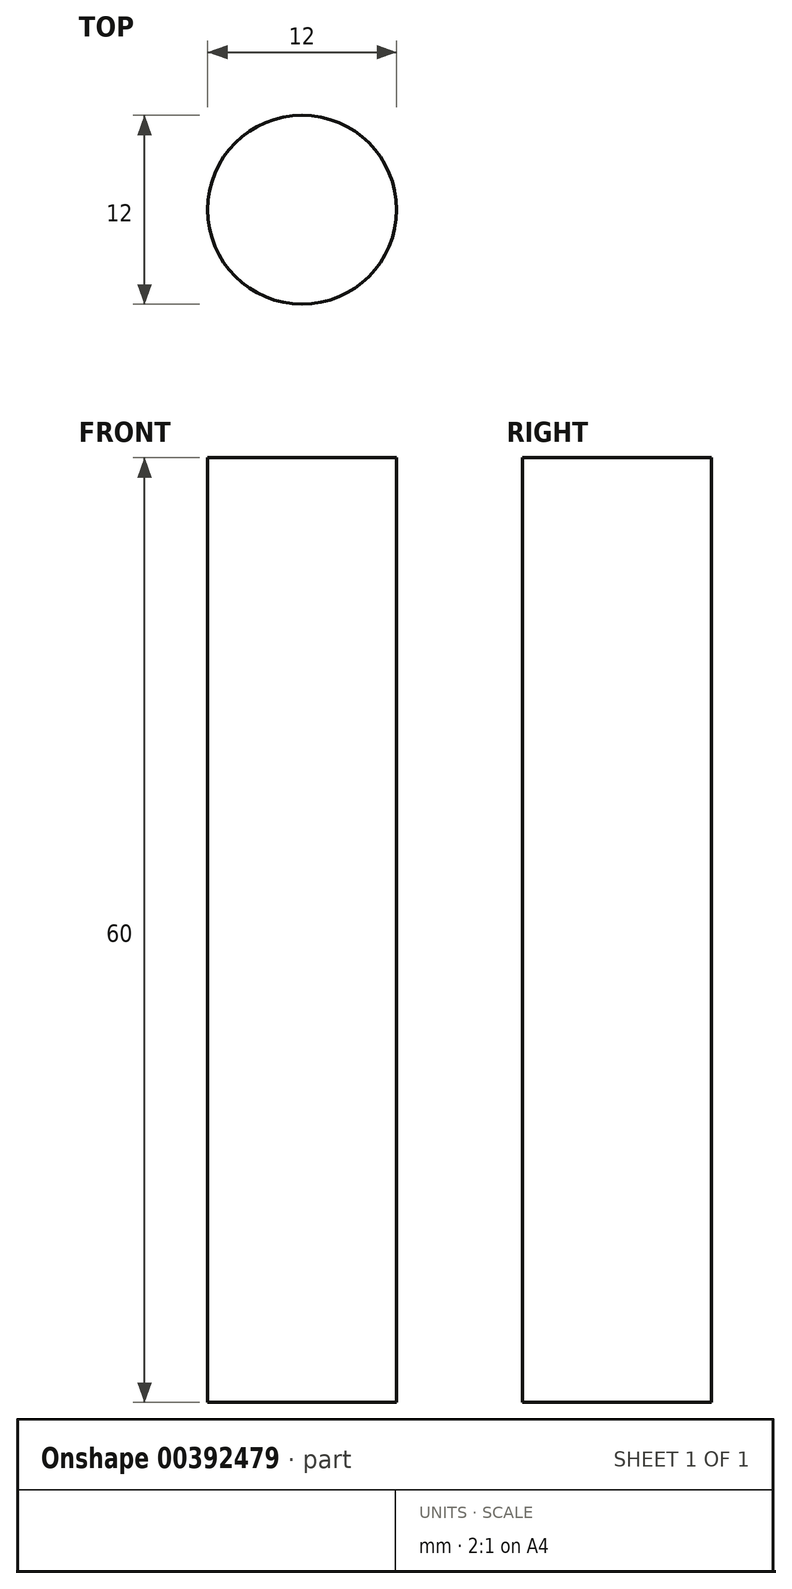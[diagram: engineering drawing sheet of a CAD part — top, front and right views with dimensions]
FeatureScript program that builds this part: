
annotation { "Feature Type Name" : "Feature", "Feature Type Description" : "" }
export const myFeature = defineFeature(function(context is Context, id is Id, definition is map)
    precondition{}
    {
        {
            var Q0;
            Q0=qCreatedBy(makeId("Top.planeOp"),FACE);
            var sketch = newSketch(context, id + "F0", { "sketchPlane" : qUnion([Q0])});
            skCircle(sketch, "E0", {"center": v(0, 0) * mm, "radius": 6 * mm});
            skSolve(sketch);
        }
        {
            var Q0;
            Q0 = qSketchRegion(id + "F0", true);
            extrude(context, id + "F1", {"entities" : qUnion([Q0]), "depth" : 60 * mm});
        }
    });
